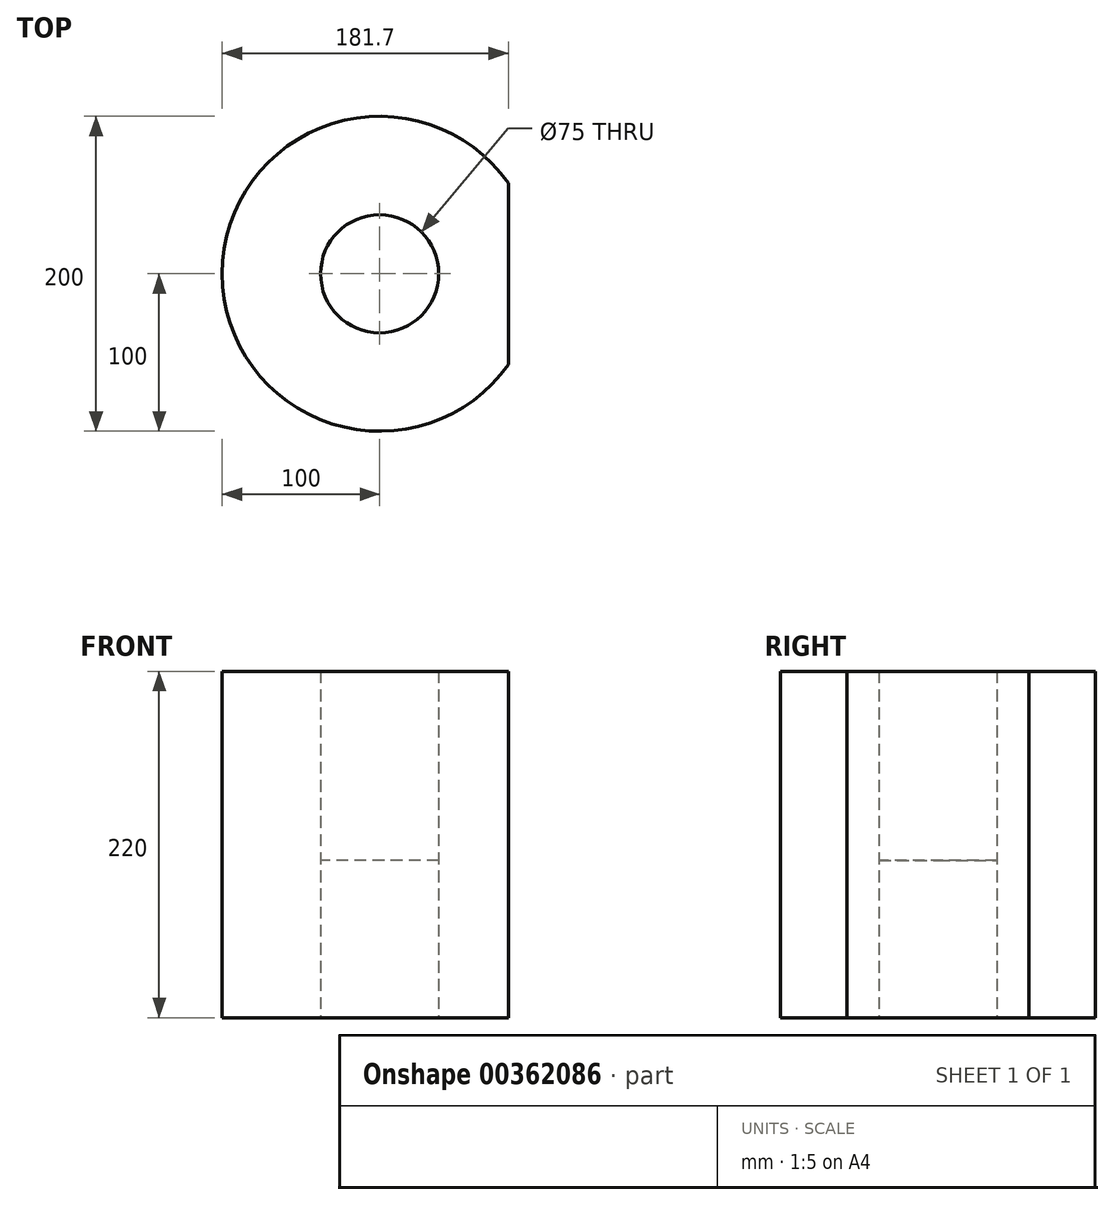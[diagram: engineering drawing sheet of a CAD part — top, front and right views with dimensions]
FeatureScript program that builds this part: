
annotation { "Feature Type Name" : "Feature", "Feature Type Description" : "" }
export const myFeature = defineFeature(function(context is Context, id is Id, definition is map)
    precondition{}
    {
        {
            var Q0;
            Q0=qCreatedBy(makeId("Top.planeOp"),FACE);
            var sketch = newSketch(context, id + "F0", { "sketchPlane" : qUnion([Q0])});
            skArc(sketch, "E0", {"start": v(81.7, 57.66) * mm, "mid": v(-100, 0) * mm, "end": v(81.7, -57.66) * mm});
            skCircle(sketch, "E1", {"center": v(0, 0) * mm, "radius": 37.5 * mm});
            skLineSegment(sketch, "E2", {"start": v(81.7, 57.66) * mm, "end": v(81.7, -57.66) * mm});
            skSolve(sketch);
        }
        {
            var Q0;
            Q0=makeQuery(id+"F0.imprint","IMPRINT",FACE,{"disambiguationData":[TD([[makeQuery(id+"F0.imprint","IMPRINT",EDGE,{"derivedFrom":sQuery(id+"F0.wireOp",EDGE,"E0")}),1.0]])]});
            extrude(context, id + "F1", {"entities" : qUnion([Q0]), "depth" : 220 * mm});
        }
        {
            var Q0;
            Q0=makeQuery(id+"F1.opExtrude","CAP_FACE",FACE,{"disambiguationData":[OSD([sQuery(id+"F0.wireOp",EDGE,"E0")])],"isStart":true});
            var sketch = newSketch(context, id + "F2", { "sketchPlane" : qUnion([Q0])});
            skSolve(sketch);
        }
        {
            var Q0;
            Q0=makeQuery(id+"F2.imprint","IMPRINT",FACE,{"disambiguationData":[TD([[makeQuery(id+"F2.imprint","IMPRINT",EDGE,{"derivedFrom":makeQuery(id+"F1.opExtrude","CAP_EDGE",EDGE,{"disambiguationData":[OSD([sQuery(id+"F0.wireOp",EDGE,"E1")])],"isStart":true})}),-1.0]])]});
            extrude(context, id + "F3", {"entities" : qUnion([Q0]), "oppositeDirection" : true, "depth" : 220 * mm});
        }
        {
            var Q0;
            Q0=makeQuery(id+"F3.opExtrude","CAP_FACE",FACE,{"disambiguationData":[OSD([sQuery(id+"F0.wireOp",EDGE,"E1")])],"isStart":true});
            extrude(context, id + "F4", {"entities" : qUnion([Q0]), "operationType" : NewBodyOperationType.REMOVE, "oppositeDirection" : true, "depth" : 100 * mm});
        }
    });
